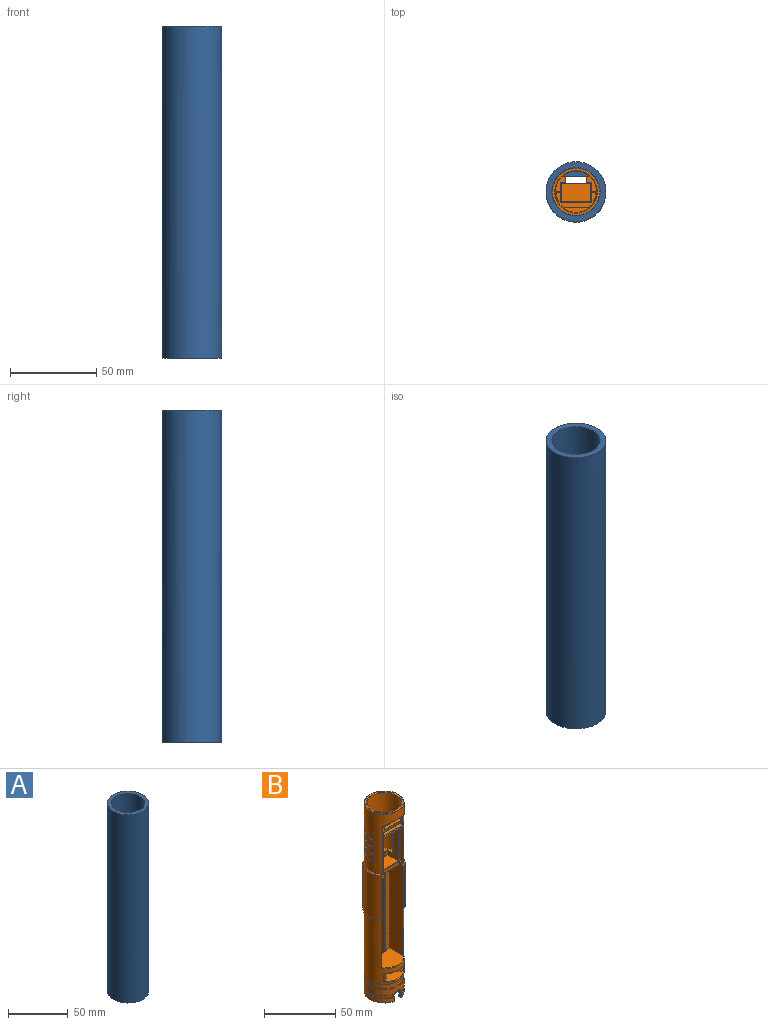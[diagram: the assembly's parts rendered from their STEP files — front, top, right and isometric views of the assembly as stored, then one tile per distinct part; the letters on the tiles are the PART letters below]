
ASSEMBLY  parts=2 mates=1
PART A: 13 faces, bbox 34.8x34.8x192.8 mm
  f0: plane 34.8x34.8mm, normal (0,0,1), area 335.4mm2, adj f2,f6
  f1: plane 34.8x34.8mm, normal (0,0,-1), area 335.4mm2, adj f2,f3
  f2: cylinder r=17.4mm len=192.8mm, axis (0,0,-1), area 21078.3mm2, adj f0,f1
  f3: cylinder r=14mm len=70.8mm, axis (0,0,-1), area 6157.8mm2, adj f1,f5,f8,f9,f10
  f4: plane 30x27.56mm, normal (0,0,-1), area 73.7mm2, adj f6,f7,f9,f10
  f5: plane 30x27.56mm, normal (0,0,1), area 73.7mm2, adj f3,f7,f9,f10
  f6: cylinder r=14mm len=82mm, axis (0,0,-1), area 7143mm2, adj f0,f4,f9,f10,f11
  f7: cylinder r=15mm len=40mm, axis (0,0,-1), area 3075.9mm2, adj f4,f5,f9,f10
  f8: plane 16.4x5mm, normal (0,0,-1), area 68.1mm2, adj f3,f9,f10,f12
  f9: plane 48x3.56mm, normal (1,0,0), area 161.2mm2, adj f3,f4,f5,f6,f7,f8,f11,f12
  f10: plane 48x3.56mm, normal (-1,0,0), area 161.2mm2, adj f3,f4,f5,f6,f7,f8,f11,f12
  f11: plane 16.4x5mm, normal (0,0,1), area 68.1mm2, adj f6,f9,f10,f12
  f12: plane 48x16.4mm, normal (0,-1,0), area 787.2mm2, adj f8,f9,f10,f11
PART B: 347 faces, bbox 32.7x30.6x163.1 mm
  f0: plane 19.04x13.2mm, normal (0,0,1), area 141.9mm2, adj f1,f335,f336,f337,f338,f339,f340,f341
  f1: plane 5.3x1.2mm, normal (0,-1,0), area 6.3mm2, adj f0,f2,f334,f335,f346
  f2: plane 15.83x14.74mm, normal (0,0,-1), area 142mm2, adj f1,f3,f4,f5,f330,f331,f332,f333
  f3: cylinder r=0.4mm len=0.86mm, axis (0,1,0), area 0.5mm2, adj f2,f4,f341,f342
  f4: torus R=0.6mm, axis (0,0,-1), area 0.3mm2, adj f2,f3,f5,f340
  f5: cylinder r=0.4mm len=2.2mm, axis (-0.92,-0.38,0), area 1.4mm2, adj f2,f4,f6,f339
  f6: bspline ~1.04x0.59mm, area 0.3mm2, adj f5,f7,f330,f339
  f7: bspline ~3.83x3.71mm, area 1.2mm2, adj f6,f8,f329,f339
  f8: bspline ~1.16x0.58mm, area 0.3mm2, adj f7,f9,f14,f15
  f9: torus R=13.6mm, axis (0,0,-1), area 6.7mm2, adj f8,f10,f15,f329
  f10: bspline ~0.97x0.62mm, area 0.3mm2, adj f9,f11,f12,f15
  f11: cylinder r=0.4mm len=7.05mm, axis (0,0,-1), area 3.3mm2, adj f10,f15,f337,f338
  f12: bspline ~3.83x3.71mm, area 1.2mm2, adj f10,f13,f329,f337
  f13: bspline ~0.97x0.58mm, area 0.3mm2, adj f12,f330,f331,f337
  f14: cylinder r=0.4mm len=7.05mm, axis (0,0,-1), area 3.3mm2, adj f8,f15,f338,f339
  f15: cylinder r=14mm len=54.5mm, axis (0,0,-1), area 3271.3mm2, adj f8,f9,f10,f11,f14,f16,f316,f317
  f16: bspline ~13.19x12.82mm, area 28.6mm2, adj f15,f17
  f17: cylinder r=6mm len=12mm, axis (0,-1,0), area 77.9mm2, adj f16,f18,f311,f312,f313,f314,f315
  f18: bspline ~2.39x0.46mm, area 0.4mm2, adj f17,f19,f315
  f19: plane 102.47x6.27mm, normal (-1,0,0), area 424.5mm2, adj f18,f20,f295,f296,f297,f306,f307,f308
  f20: cylinder r=0.4mm len=1.61mm, axis (0,-1,0), area 0.8mm2, adj f19,f21,f294,f310
  f21: plane 21.42x18.8mm, normal (0,0,1), area 349.1mm2, adj f20,f22,f290,f291,f292,f293,f294,f325
  f22: plane 77.6x14mm, normal (-1,0,0), area 1050.7mm2, adj f21,f23,f287,f288,f289,f293,f327
  f23: cylinder r=0.4mm len=21.1mm, axis (1,0,0), area 13.3mm2, adj f22,f24,f287,f290,f291,f293
  f24: plane 12.8x3mm, normal (0,1,0), area 38.4mm2, adj f23,f25,f286,f310
  f25: cylinder r=0.2mm len=17.2mm, axis (1,0,0), area 5.4mm2, adj f24,f26,f282,f283,f284,f285
  f26: plane 36.8x11.2mm, normal (-1,0,0), area 213mm2, adj f25,f27,f273,f274,f275,f276,f277,f278
  f27: cylinder r=0.2mm len=5.8mm, axis (0,1,0), area 1.7mm2, adj f26,f28,f30,f273
  f28: cylinder r=0.2mm len=2.4mm, axis (-1,0,0), area 0.7mm2, adj f27,f29,f30,f285
  f29: torus R=0.2mm, axis (0,0,1), area 0.2mm2, adj f28,f30,f309,f310
  f30: plane 8.85x5.79mm, normal (0,0,1), area 26.5mm2, adj f27,f28,f29,f31,f269,f270,f271,f272
  f31: cylinder r=0.4mm len=32.6mm, axis (0,0,1), area 20.9mm2, adj f30,f32,f269,f272
  f32: bspline ~0.98x0.97mm, area 0.6mm2, adj f31,f33,f268,f272
  f33: cylinder r=0.4mm len=2.59mm, axis (-1,0,0), area 1.6mm2, adj f32,f34,f267,f269
  f34: plane 23.19x8.4mm, normal (0,0,1), area 65.2mm2, adj f33,f35,f263,f264,f265,f266,f268,f274
  f35: cylinder r=0.4mm len=15.11mm, axis (-1,0,0), area 9.5mm2, adj f34,f36,f261,f262
  f36: plane 80.11x23.32mm, normal (0,-1,0), area 142.8mm2, adj f35,f37,f45,f48,f49,f50,f54,f55
  f37: cylinder r=0.4mm len=3.6mm, axis (0,0,1), area 2.1mm2, adj f36,f38,f44,f45
  f38: plane 3.2x3.2mm, normal (-1,0,0), area 9mm2, adj f37,f39,f43,f44,f45
  f39: plane 17.2x2.8mm, normal (0,-1,0), area 48.2mm2, adj f38,f40,f42,f43
  f40: cylinder r=0.4mm len=18mm, axis (1,0,0), area 11.1mm2, adj f39,f41,f44,f287
  f41: cylinder r=0.4mm len=3.6mm, axis (0,1,0), area 2mm2, adj f40,f42,f55,f287
  f42: plane 3.2x3.2mm, normal (1,0,0), area 9mm2, adj f39,f41,f43,f54,f55
  f43: cylinder r=0.4mm len=17.2mm, axis (-1,0,0), area 10.8mm2, adj f38,f39,f42,f282
  f44: cylinder r=0.4mm len=3.6mm, axis (0,-1,0), area 2mm2, adj f37,f38,f40,f287
  f45: plane 3.6x1.8mm, normal (0,0,1), area 4.5mm2, adj f36,f37,f38,f46,f47,f48,f281
  f46: plane 30x1mm, normal (0,-1,0), area 30mm2, adj f45,f47,f280,f281
  f47: plane 30x2.8mm, normal (-1,0,0), area 84.1mm2, adj f45,f46,f48,f280
  f48: cylinder r=0.4mm len=30.4mm, axis (0,0,-1), area 19mm2, adj f36,f45,f47,f49
  f49: cylinder r=0.4mm len=20.8mm, axis (1,0,0), area 12.8mm2, adj f36,f48,f50,f280
  f50: cylinder r=0.4mm len=30.4mm, axis (0,0,1), area 19mm2, adj f36,f49,f51,f54
  f51: plane 30x2.8mm, normal (1,0,0), area 84.1mm2, adj f50,f52,f54,f280
  f52: plane 30x1mm, normal (0,-1,0), area 30mm2, adj f51,f53,f54,f280
  f53: cylinder r=0.4mm len=30mm, axis (0,0,-1), area 18.8mm2, adj f52,f54,f280,f283
  f54: plane 3.6x1.8mm, normal (0,0,1), area 4.5mm2, adj f36,f42,f50,f51,f52,f53,f55
  f55: cylinder r=0.4mm len=3.6mm, axis (0,0,-1), area 2.1mm2, adj f36,f41,f42,f54
  f56: cylinder r=0.4mm len=35.78mm, axis (0,0,-1), area 22.5mm2, adj f36,f57,f287,f290
  f57: sphere r=0.4mm, area 0.2mm2, adj f56,f58,f59
  f58: bspline ~4.34x3.12mm, area 0.7mm2, adj f57,f290,f324,f325
  f59: bspline ~5.05x4.14mm, area 0.4mm2, adj f36,f57,f60,f324
  f60: sphere r=0.4mm, area 0.1mm2, adj f59,f61,f201
  f61: torus R=14.6mm, axis (0,0,-1), area 7.5mm2, adj f60,f62,f200,f324
  f62: sphere r=0.4mm, area 0.2mm2, adj f61,f63,f199
  f63: cylinder r=0.4mm len=37.67mm, axis (0,0,-1), area 33.2mm2, adj f62,f64,f197,f200
  f64: plane 48x2.8mm, normal (1,0,0), area 122.5mm2, adj f63,f65,f193,f194,f195,f196,f199,f322
  f65: plane 16.57x4.65mm, normal (0,0,1), area 41.4mm2, adj f64,f66,f178,f179,f191,f192,f193,f307
  f66: cylinder r=0.2mm len=1.99mm, axis (0,1,0), area 0.5mm2, adj f65,f67,f178,f192
  f67: plane 102.47x6.27mm, normal (1,0,0), area 424.5mm2, adj f66,f68,f166,f178,f286,f292,f295,f297
  f68: cylinder r=0.4mm len=6.4mm, axis (0,-1,0), area 3.8mm2, adj f67,f69,f79,f80
  f69: plane 24x22.15mm, normal (0,0,-1), area 317.6mm2, adj f68,f70,f73,f74,f76,f79,f80,f296
  f70: cylinder r=0.4mm len=1.85mm, axis (1,0,0), area 1mm2, adj f69,f71,f295,f296
  f71: sphere r=0.4mm, area 0.2mm2, adj f70,f72,f73
  f72: cylinder r=0.4mm len=11.65mm, axis (0,0,1), area 7.2mm2, adj f71,f295,f333,f346
  f73: cylinder r=0.4mm len=4.39mm, axis (0,1,0), area 2.6mm2, adj f69,f71,f74,f346
  f74: cylinder r=0.4mm len=9.1mm, axis (1,0,0), area 5.5mm2, adj f69,f73,f75,f76
  f75: plane 8.3x5.55mm, normal (0,1,0), area 46.1mm2, adj f74,f344,f345,f346
  f76: cylinder r=0.4mm len=4.39mm, axis (0,-1,0), area 2.6mm2, adj f69,f74,f77,f344
  f77: sphere r=0.4mm, area 0.2mm2, adj f76,f78,f79
  f78: cylinder r=0.4mm len=11.65mm, axis (0,0,-1), area 7.2mm2, adj f77,f295,f333,f344
  f79: cylinder r=0.4mm len=1.85mm, axis (1,0,0), area 1mm2, adj f68,f69,f77,f295
  f80: cylinder r=12mm len=24mm, axis (0,0,-1), area 778mm2, adj f68,f69,f81,f158,f159,f160,f161,f162
  f81: cylinder r=0.4mm len=4.6mm, axis (0,0,-1), area 2.4mm2, adj f80,f82,f157,f165
  f82: sphere r=0.4mm, area 0.1mm2, adj f81,f83,f159
  f83: cylinder r=0.4mm len=1.24mm, axis (0,-1,0), area 0.8mm2, adj f82,f84,f85,f156,f157
  f84: sphere r=0.4mm, area 0mm2, adj f83,f159
  f85: plane 26.34x10.2mm, normal (0,0,-1), area 40.8mm2, adj f83,f86,f155,f159
  f86: cylinder r=0.4mm len=1.24mm, axis (0,-1,0), area 0.8mm2, adj f85,f87,f153,f154
  f87: plane 4.6x1.24mm, normal (1,0,0), area 4.9mm2, adj f86,f88,f150,f151,f152,f160
  f88: cylinder r=0.4mm len=3.3mm, axis (0,0,-1), area 2.4mm2, adj f87,f89,f148,f149,f153
  f89: cylinder r=14mm len=27.11mm, axis (0,0,-1), area 121.8mm2, adj f88,f90,f147,f155
  f90: torus R=13.7mm, axis (0,0,-1), area 17.3mm2, adj f89,f91,f146,f149
  f91: plane 26.54x10.3mm, normal (0,0,1), area 10.7mm2, adj f90,f92,f143,f144,f146,f149,f151,f152
  f92: cylinder r=13.4mm len=25.95mm, axis (0,0,1), area 70.2mm2, adj f91,f93,f141,f142,f143,f151
  f93: bspline ~2.51x0.94mm, area 0.8mm2, adj f92,f94,f141,f150,f151
  f94: cylinder r=0.4mm len=0.7mm, axis (0,-1,0), area 0.2mm2, adj f93,f95,f141,f150
  f95: bspline ~0.43x0.38mm, area 0.1mm2, adj f94,f96,f140
  f96: bspline ~6.78x2.7mm, area 4.9mm2, adj f95,f97,f134,f135,f140,f150
  f97: bspline ~0.43x0.38mm, area 0.1mm2, adj f96,f98,f134
  f98: cylinder r=0.4mm len=0.7mm, axis (0,-1,0), area 0.2mm2, adj f97,f99,f133,f150
  f99: bspline ~2.51x0.94mm, area 0.8mm2, adj f98,f100,f132,f133,f150
  f100: cylinder r=13.4mm len=25.95mm, axis (0,0,1), area 70.2mm2, adj f99,f101,f130,f131,f132,f133
  f101: plane 26.54x10.4mm, normal (0,0,1), area 10.8mm2, adj f100,f102,f126,f127,f128,f129,f130,f132
  f102: cylinder r=0.3mm len=0.62mm, axis (0,1,0), area 0.2mm2, adj f101,f103,f126,f132
  f103: plane 4.6x1.24mm, normal (-1,0,0), area 4.9mm2, adj f102,f104,f125,f132,f150,f162
  f104: cylinder r=0.4mm len=1.24mm, axis (0,1,0), area 0.8mm2, adj f103,f105,f106,f124
  f105: sphere r=0.4mm, area 0.1mm2, adj f104,f162,f163
  f106: plane 26.34x10.2mm, normal (0,0,-1), area 40.8mm2, adj f104,f107,f123,f163
  f107: cylinder r=0.4mm len=1.24mm, axis (0,1,0), area 0.8mm2, adj f106,f108,f109,f122
  f108: sphere r=0.4mm, area 0.3mm2, adj f107,f163,f164
  f109: plane 4.6x1.24mm, normal (-1,0,0), area 4.9mm2, adj f107,f110,f120,f129,f130,f164
  f110: cylinder r=3mm len=6mm, axis (0,-1,0), area 10mm2, adj f109,f111,f115,f119,f131,f142,f157,f165
  f111: cylinder r=0.4mm len=0.7mm, axis (0,-1,0), area 0.2mm2, adj f110,f112,f131,f133
  f112: bspline ~0.43x0.38mm, area 0.1mm2, adj f111,f113,f115
  f113: bspline ~0.36x0.33mm, area 0.1mm2, adj f112,f114,f115,f133
  f114: torus R=13.7mm, axis (0,0,-1), area 17.5mm2, adj f113,f133,f134,f135
  f115: bspline ~6.78x2.7mm, area 4.9mm2, adj f110,f112,f113,f116,f117,f135
  f116: bspline ~0.43x0.38mm, area 0.1mm2, adj f115,f117,f119
  f117: bspline ~0.41x0.33mm, area 0.1mm2, adj f115,f116,f118,f141
  f118: torus R=13.7mm, axis (0,0,-1), area 17.5mm2, adj f117,f135,f140,f141
  f119: cylinder r=0.4mm len=0.7mm, axis (0,-1,0), area 0.2mm2, adj f110,f116,f141,f142
  f120: cylinder r=0.4mm len=3.3mm, axis (0,0,-1), area 2.4mm2, adj f109,f121,f122,f128
  f121: cylinder r=14mm len=27.11mm, axis (0,0,-1), area 121.8mm2, adj f120,f123,f125,f127
  f122: sphere r=0.4mm, area 0.4mm2, adj f107,f120,f123
  f123: torus R=13.6mm, axis (0,0,-1), area 22.9mm2, adj f106,f121,f122,f124
  f124: sphere r=0.4mm, area 0.3mm2, adj f104,f123,f125
  f125: cylinder r=0.4mm len=3.3mm, axis (0,0,-1), area 2.4mm2, adj f103,f121,f124,f126
  f126: torus R=0.1mm, axis (0,0,-1), area 0.3mm2, adj f101,f102,f125,f127
  f127: torus R=13.7mm, axis (0,0,-1), area 17.3mm2, adj f101,f121,f126,f128
  f128: torus R=0.1mm, axis (0,0,-1), area 0.3mm2, adj f101,f120,f127,f129
  f129: cylinder r=0.3mm len=0.62mm, axis (0,1,0), area 0.2mm2, adj f101,f109,f128,f130
  f130: cylinder r=0.4mm len=1.3mm, axis (0,0,1), area 0.8mm2, adj f100,f101,f109,f129,f131
  f131: bspline ~2.51x0.94mm, area 0.8mm2, adj f100,f110,f111,f130,f133
  f132: cylinder r=0.4mm len=1.3mm, axis (0,0,1), area 0.8mm2, adj f99,f100,f101,f102,f103
  f133: plane 26.68x10.61mm, normal (0,0,-1), area 10.9mm2, adj f98,f99,f100,f111,f113,f114,f131,f134
  f134: bspline ~0.41x0.33mm, area 0.1mm2, adj f96,f97,f114,f133
  f135: cylinder r=14mm len=28mm, axis (0,0,-1), area 475mm2, adj f96,f114,f115,f118,f136
  f136: torus R=13.7mm, axis (0,0,-1), area 41.1mm2, adj f135,f137
  f137: plane 27.4x27.4mm, normal (0,0,1), area 25.5mm2, adj f136,f138
  f138: cylinder r=13.4mm len=26.8mm, axis (0,0,1), area 336.8mm2, adj f137,f139
  f139: plane 27.4x27.4mm, normal (0,0,-1), area 25.5mm2, adj f138,f323
  f140: bspline ~0.36x0.33mm, area 0.1mm2, adj f95,f96,f118,f141
  f141: plane 26.68x10.61mm, normal (0,0,-1), area 10.9mm2, adj f92,f93,f94,f117,f118,f119,f140,f142
  f142: bspline ~2.51x0.94mm, area 0.8mm2, adj f92,f110,f119,f141,f143
  f143: cylinder r=0.4mm len=1.4mm, axis (0,0,1), area 0.8mm2, adj f91,f92,f142,f144,f157
  f144: cylinder r=0.4mm len=0.72mm, axis (0,-1,0), area 0.3mm2, adj f91,f143,f145,f157
  f145: bspline ~0.49x0.4mm, area 0.1mm2, adj f144,f146,f147
  f146: torus R=0.1mm, axis (0,0,-1), area 0mm2, adj f90,f91,f145,f147
  f147: cylinder r=0.4mm len=3.3mm, axis (0,0,-1), area 2.4mm2, adj f89,f145,f146,f156,f157
  f148: bspline ~0.49x0.4mm, area 0.1mm2, adj f88,f149,f152
  f149: torus R=0.1mm, axis (0,0,-1), area 0mm2, adj f88,f90,f91,f148
  f150: cylinder r=3mm len=6mm, axis (0,-1,0), area 10mm2, adj f87,f93,f94,f96,f98,f99,f103,f161
  f151: cylinder r=0.4mm len=1.4mm, axis (0,0,1), area 0.8mm2, adj f87,f91,f92,f93,f152
  f152: cylinder r=0.4mm len=0.72mm, axis (0,-1,0), area 0.3mm2, adj f87,f91,f148,f151
  f153: sphere r=0.4mm, area 0.2mm2, adj f86,f88,f155
  f154: sphere r=0.4mm, area 0.3mm2, adj f86,f159,f160
  f155: torus R=13.6mm, axis (0,0,-1), area 22.9mm2, adj f85,f89,f153,f156
  f156: sphere r=0.4mm, area 0.4mm2, adj f83,f147,f155
  f157: plane 4.6x1.24mm, normal (1,0,0), area 4.9mm2, adj f81,f83,f110,f143,f144,f147
  f158: plane 12x1.61mm, normal (0,0,-1), area 13mm2, adj f80,f297
  f159: torus R=12.4mm, axis (0,0,-1), area 19.7mm2, adj f80,f82,f84,f85,f154
  f160: cylinder r=0.4mm len=4.6mm, axis (0,0,-1), area 2.4mm2, adj f80,f87,f154,f161
  f161: bspline ~6.58x4.15mm, area 5.6mm2, adj f80,f150,f160,f162
  f162: cylinder r=0.4mm len=4.6mm, axis (0,0,-1), area 2.4mm2, adj f80,f103,f105,f161
  f163: torus R=12.4mm, axis (0,0,-1), area 19.7mm2, adj f80,f105,f106,f108
  f164: cylinder r=0.4mm len=4.6mm, axis (0,0,-1), area 2.4mm2, adj f80,f108,f109,f165
  f165: bspline ~6.58x4.15mm, area 5.6mm2, adj f80,f81,f110,f164
  f166: cylinder r=0.2mm len=3mm, axis (0,-1,0), area 0.9mm2, adj f67,f167,f176,f177
  f167: plane 8.85x5.79mm, normal (0,0,1), area 26.5mm2, adj f166,f168,f169,f170,f172,f173,f175,f176
  f168: cylinder r=0.2mm len=2.4mm, axis (-1,0,0), area 0.7mm2, adj f167,f169,f177,f284
  f169: cylinder r=0.2mm len=5.8mm, axis (0,1,0), area 1.7mm2, adj f167,f168,f170,f283
  f170: cylinder r=0.4mm len=32.8mm, axis (0,0,1), area 20.5mm2, adj f167,f169,f171,f172,f283
  f171: sphere r=0.4mm, area 0.3mm2, adj f170,f264,f265
  f172: plane 32.6x2.59mm, normal (0,1,0), area 84.5mm2, adj f167,f170,f173,f264
  f173: cylinder r=0.4mm len=32.6mm, axis (0,0,1), area 20.9mm2, adj f167,f172,f174,f272
  f174: bspline ~1.01x0.94mm, area 0.6mm2, adj f173,f263,f264,f272
  f175: cylinder r=0.2mm len=1.76mm, axis (1,0,0), area 0.5mm2, adj f167,f176,f193,f272
  f176: torus R=0.2mm, axis (0,0,1), area 0.2mm2, adj f166,f167,f175,f178
  f177: torus R=0.2mm, axis (0,0,1), area 0.2mm2, adj f166,f167,f168,f286
  f178: cylinder r=0.4mm len=48mm, axis (0,0,-1), area 30.1mm2, adj f65,f66,f67,f176,f193
  f179: plane 48x2.8mm, normal (-1,0,0), area 122.5mm2, adj f65,f180,f187,f188,f190,f191,f194,f320
  f180: cylinder r=0.4mm len=37.67mm, axis (0,0,-1), area 33.2mm2, adj f179,f181,f184,f186
  f181: sphere r=0.4mm, area 0.2mm2, adj f180,f182,f190
  f182: torus R=14.6mm, axis (0,0,-1), area 7.5mm2, adj f181,f183,f184,f328
  f183: sphere r=0.4mm, area 0.1mm2, adj f182,f249,f250
  f184: cylinder r=15mm len=37.67mm, axis (0,0,-1), area 897.3mm2, adj f180,f182,f185,f249
  f185: torus R=14.6mm, axis (0,0,1), area 7.5mm2, adj f184,f186,f248,f249
  f186: sphere r=0.4mm, area 0.3mm2, adj f180,f185,f187
  f187: bspline ~5.08x4.26mm, area 1.2mm2, adj f179,f186,f188,f248
  f188: cylinder r=0.4mm len=4.57mm, axis (0,0,-1), area 3.7mm2, adj f179,f187,f189,f194,f208,f248
  f189: torus R=13.6mm, axis (0,0,1), area 11.7mm2, adj f188,f194,f195,f208
  f190: bspline ~5.08x4.26mm, area 1.2mm2, adj f179,f181,f320,f328
  f191: plane 48x1.8mm, normal (0,1,0), area 86.1mm2, adj f65,f179,f194,f271,f272,f308
  f192: cylinder r=0.2mm len=12.4mm, axis (1,0,0), area 3.8mm2, adj f65,f66,f306,f307
  f193: plane 48x1.8mm, normal (0,1,0), area 86.1mm2, adj f64,f65,f175,f178,f194,f272
  f194: plane 16.57x4.6mm, normal (0,0,-1), area 28.5mm2, adj f64,f179,f188,f189,f191,f193,f195,f272
  f195: cylinder r=0.4mm len=4.57mm, axis (0,0,-1), area 3.7mm2, adj f64,f189,f194,f196,f202,f208
  f196: bspline ~5.08x4.26mm, area 1.2mm2, adj f64,f195,f197,f202
  f197: sphere r=0.4mm, area 0.3mm2, adj f63,f196,f198
  f198: torus R=14.6mm, axis (0,0,1), area 7.5mm2, adj f197,f200,f201,f202
  f199: bspline ~5.08x4.26mm, area 1.2mm2, adj f62,f64,f322,f324
  f200: cylinder r=15mm len=37.67mm, axis (0,0,-1), area 897.3mm2, adj f61,f63,f198,f201
  f201: cylinder r=0.4mm len=37.99mm, axis (0,0,-1), area 14mm2, adj f36,f60,f198,f200,f202
  f202: cone r=14mm half-angle=45deg, axis (0,0,-1), area 29mm2, adj f36,f195,f196,f198,f201,f208
  f203: cylinder r=0.4mm len=3.17mm, axis (0,0,1), area 2.8mm2, adj f36,f204,f206,f261,f272
  f204: bspline ~17.47x4.15mm, area 17.8mm2, adj f203,f205,f206,f272
  f205: cylinder r=0.4mm len=3.17mm, axis (0,0,1), area 2.8mm2, adj f36,f204,f206,f262,f272
  f206: plane 20.52x4.69mm, normal (0,-0.68,-0.73), area 34.6mm2, adj f36,f203,f204,f205,f207
  f207: bspline ~21.19x4.85mm, area 9.5mm2, adj f36,f206,f208
  f208: cylinder r=14mm len=51.6mm, axis (0,0,-1), area 2458.5mm2, adj f36,f188,f189,f195,f202,f207,f209,f215
  f209: cylinder r=0.3mm len=4.6mm, axis (0,0,-1), area 2mm2, adj f208,f210,f213,f214,f215,f217
  f210: plane 27.4x17.25mm, normal (0,0,1), area 14.9mm2, adj f209,f211,f212,f214,f215,f216
  f211: cylinder r=13.4mm len=26.8mm, axis (0,0,1), area 196.5mm2, adj f210,f212,f213,f214
  f212: plane 4x0.29mm, normal (-0.26,0.97,0), area 1.2mm2, adj f210,f211,f213,f216
  f213: plane 27.4x17.25mm, normal (0,0,-1), area 14.9mm2, adj f209,f211,f212,f214,f216,f217
  f214: plane 4x0.29mm, normal (0.26,0.97,0), area 1.2mm2, adj f209,f210,f211,f213
  f215: torus R=13.7mm, axis (0,0,-1), area 24.1mm2, adj f208,f209,f210,f216
  f216: cylinder r=0.3mm len=4.6mm, axis (0,0,-1), area 2mm2, adj f208,f210,f212,f213,f215,f217
  f217: torus R=13.7mm, axis (0,0,-1), area 24.1mm2, adj f208,f209,f213,f216
  f218: cylinder r=0.3mm len=4.6mm, axis (0,0,-1), area 2mm2, adj f208,f219,f222,f223,f224,f226
  f219: plane 27.4x17.25mm, normal (0,0,1), area 14.9mm2, adj f218,f220,f221,f223,f224,f225
  f220: cylinder r=13.4mm len=26.8mm, axis (0,0,1), area 196.5mm2, adj f219,f221,f222,f223
  f221: plane 4x0.29mm, normal (-0.26,0.97,0), area 1.2mm2, adj f219,f220,f222,f225
  f222: plane 27.4x17.25mm, normal (0,0,-1), area 14.9mm2, adj f218,f220,f221,f223,f225,f226
  f223: plane 4x0.29mm, normal (0.26,0.97,0), area 1.2mm2, adj f218,f219,f220,f222
  f224: torus R=13.7mm, axis (0,0,-1), area 24.1mm2, adj f208,f218,f219,f225
  f225: cylinder r=0.3mm len=4.6mm, axis (0,0,-1), area 2mm2, adj f208,f219,f221,f222,f224,f226
  f226: torus R=13.7mm, axis (0,0,-1), area 24.1mm2, adj f208,f218,f222,f225
  f227: cylinder r=0.3mm len=4.6mm, axis (0,0,-1), area 2mm2, adj f208,f228,f231,f232,f233,f235
  f228: plane 27.4x17.25mm, normal (0,0,1), area 14.9mm2, adj f227,f229,f230,f232,f233,f234
  f229: cylinder r=13.4mm len=26.8mm, axis (0,0,1), area 196.5mm2, adj f228,f230,f231,f232
  f230: plane 4x0.29mm, normal (-0.26,0.97,0), area 1.2mm2, adj f228,f229,f231,f234
  f231: plane 27.4x17.25mm, normal (0,0,-1), area 14.9mm2, adj f227,f229,f230,f232,f234,f235
  f232: plane 4x0.29mm, normal (0.26,0.97,0), area 1.2mm2, adj f227,f228,f229,f231
  f233: torus R=13.7mm, axis (0,0,-1), area 24.1mm2, adj f208,f227,f228,f234
  f234: cylinder r=0.3mm len=4.6mm, axis (0,0,-1), area 2mm2, adj f208,f228,f230,f231,f233,f235
  f235: torus R=13.7mm, axis (0,0,-1), area 24.1mm2, adj f208,f227,f231,f234
  f236: cylinder r=0.3mm len=4.6mm, axis (0,0,-1), area 2mm2, adj f208,f237,f240,f241,f242,f244
  f237: plane 27.4x17.25mm, normal (0,0,1), area 14.9mm2, adj f236,f238,f239,f241,f242,f243
  f238: cylinder r=13.4mm len=26.8mm, axis (0,0,1), area 196.5mm2, adj f237,f239,f240,f241
  f239: plane 4x0.29mm, normal (-0.26,0.97,0), area 1.2mm2, adj f237,f238,f240,f243
  f240: plane 27.4x17.25mm, normal (0,0,-1), area 14.9mm2, adj f236,f238,f239,f241,f243,f244
  f241: plane 4x0.29mm, normal (0.26,0.97,0), area 1.2mm2, adj f236,f237,f238,f240
  f242: torus R=13.7mm, axis (0,0,-1), area 24.1mm2, adj f208,f236,f237,f243
  f243: cylinder r=0.3mm len=4.6mm, axis (0,0,-1), area 2mm2, adj f208,f237,f239,f240,f242,f244
  f244: torus R=13.7mm, axis (0,0,-1), area 24.1mm2, adj f208,f236,f240,f243
  f245: torus R=13.6mm, axis (0,0,1), area 54.7mm2, adj f208,f246
  f246: plane 27.2x27.2mm, normal (0,0,1), area 98mm2, adj f245,f247
  f247: torus R=12.4mm, axis (0,0,1), area 47.9mm2, adj f246,f272
  f248: cone r=14mm half-angle=45deg, axis (0,0,-1), area 29mm2, adj f36,f185,f187,f188,f208,f249
  f249: cylinder r=0.4mm len=37.99mm, axis (0,0,-1), area 14mm2, adj f36,f183,f184,f185,f248
  f250: bspline ~5.05x4.14mm, area 0.4mm2, adj f36,f183,f251,f328
  f251: sphere r=0.4mm, area 0.2mm2, adj f250,f288,f289
  f252: cylinder r=0.4mm len=20.8mm, axis (-1,0,0), area 12.8mm2, adj f36,f253,f257,f278
  f253: cylinder r=0.4mm len=3.8mm, axis (0,0,-1), area 2.1mm2, adj f36,f252,f254,f256
  f254: plane 3x2.8mm, normal (-1,0,0), area 8.4mm2, adj f253,f255,f276,f278
  f255: plane 3x1mm, normal (0,-1,0), area 3mm2, adj f254,f276,f277,f278
  f256: cylinder r=0.4mm len=20.8mm, axis (1,0,0), area 12.8mm2, adj f36,f253,f257,f276
  f257: cylinder r=0.4mm len=3.8mm, axis (0,0,1), area 2.1mm2, adj f36,f252,f256,f258
  f258: plane 3x2.8mm, normal (1,0,0), area 8.4mm2, adj f257,f259,f276,f278
  f259: plane 3x1mm, normal (0,-1,0), area 3mm2, adj f258,f260,f276,f278
  f260: cylinder r=0.4mm len=3mm, axis (0,0,-1), area 1.9mm2, adj f259,f276,f278,f283
  f261: bspline ~1.6x0.95mm, area 0.9mm2, adj f35,f36,f203,f263
  f262: bspline ~1.43x0.95mm, area 0.9mm2, adj f35,f36,f205,f268
  f263: torus R=11.6mm, axis (0,0,1), area 5.9mm2, adj f34,f174,f261,f272
  f264: cylinder r=0.4mm len=2.59mm, axis (-1,0,0), area 1.6mm2, adj f34,f171,f172,f174
  f265: cylinder r=0.4mm len=6mm, axis (0,-1,0), area 3.6mm2, adj f34,f171,f266,f283
  f266: cylinder r=0.4mm len=18mm, axis (1,0,0), area 11.1mm2, adj f34,f265,f274,f275
  f267: sphere r=0.4mm, area 0.4mm2, adj f33,f273,f274
  f268: torus R=11.6mm, axis (0,0,1), area 5.9mm2, adj f32,f34,f262,f272
  f269: plane 32.6x2.59mm, normal (0,1,0), area 84.5mm2, adj f30,f31,f33,f273
  f270: torus R=0.2mm, axis (0,0,1), area 0.2mm2, adj f30,f271,f308,f309
  f271: cylinder r=0.2mm len=1.76mm, axis (1,0,0), area 0.5mm2, adj f30,f191,f270,f272
  f272: cylinder r=12mm len=47.8mm, axis (0,0,1), area 2201.7mm2, adj f30,f31,f32,f167,f173,f174,f175,f191
  f273: cylinder r=0.4mm len=32.8mm, axis (0,0,-1), area 20.5mm2, adj f26,f27,f30,f267,f269
  f274: cylinder r=0.4mm len=6mm, axis (0,1,0), area 3.6mm2, adj f26,f34,f266,f267
  f275: plane 17.2x1.6mm, normal (0,1,0), area 27.5mm2, adj f26,f266,f276,f283
  f276: plane 20x3.2mm, normal (0,0,-1), area 56.1mm2, adj f26,f254,f255,f256,f258,f259,f260,f275
  f277: cylinder r=0.4mm len=3mm, axis (0,0,-1), area 1.9mm2, adj f26,f255,f276,f278
  f278: plane 20x3.2mm, normal (0,0,1), area 56.1mm2, adj f26,f252,f254,f255,f258,f259,f260,f277
  f279: plane 17.2x2mm, normal (0,1,0), area 34.4mm2, adj f26,f278,f280,f283
  f280: plane 20x3.2mm, normal (0,0,-1), area 56.1mm2, adj f26,f46,f47,f49,f51,f52,f53,f279
  f281: cylinder r=0.4mm len=30mm, axis (0,0,-1), area 18.8mm2, adj f26,f45,f46,f280
  f282: plane 17.2x10.6mm, normal (0,0,1), area 182.3mm2, adj f25,f26,f43,f283
  f283: plane 36.8x11.2mm, normal (1,0,0), area 213mm2, adj f25,f53,f169,f170,f260,f265,f275,f276
  f284: plane 4x2.2mm, normal (0,-1,0), area 8.8mm2, adj f25,f168,f283,f286
  f285: plane 4x2.2mm, normal (0,-1,0), area 8.8mm2, adj f25,f26,f28,f310
  f286: cylinder r=0.4mm len=85mm, axis (0,0,1), area 53.3mm2, adj f24,f67,f177,f284,f291,f292
  f287: plane 21.9x14mm, normal (0,0,-1), area 230.7mm2, adj f22,f23,f36,f40,f41,f44,f56,f288
  f288: cylinder r=0.4mm len=35.78mm, axis (0,0,1), area 22.5mm2, adj f22,f36,f251,f287
  f289: bspline ~4.34x3.12mm, area 0.7mm2, adj f22,f251,f327,f328
  f290: plane 77.6x14mm, normal (1,0,0), area 1050.7mm2, adj f21,f23,f56,f58,f287,f291,f325
  f291: plane 77.6x4.15mm, normal (0,-1,0), area 322mm2, adj f21,f23,f286,f290
  f292: cylinder r=0.4mm len=1.61mm, axis (0,1,0), area 0.8mm2, adj f21,f67,f286,f294
  f293: plane 77.6x4.15mm, normal (0,-1,0), area 322mm2, adj f21,f22,f23,f310
  f294: cylinder r=0.4mm len=12.8mm, axis (-1,0,0), area 7.8mm2, adj f20,f21,f292,f295
  f295: plane 17.2x12mm, normal (0,1,0), area 100.4mm2, adj f19,f67,f70,f72,f78,f79,f294,f333
  f296: cylinder r=0.4mm len=6.4mm, axis (0,1,0), area 3.8mm2, adj f19,f69,f70,f80
  f297: plane 34.17x12mm, normal (0,-1,0), area 330.3mm2, adj f19,f67,f80,f158,f298,f303,f304,f305
  f298: cylinder r=0.4mm len=6.1mm, axis (0,0,1), area 3.6mm2, adj f297,f299,f303,f305
  f299: plane 5.3x2.34mm, normal (1,0,0), area 12.4mm2, adj f298,f300,f302,f316
  f300: plane 6.32x2.81mm, normal (0,0,-1), area 16.9mm2, adj f299,f301,f305,f316,f317,f318
  f301: plane 5.3x2.34mm, normal (-1,0,0), area 12.4mm2, adj f300,f302,f304,f318
  f302: plane 6.32x2.81mm, normal (0,0,1), area 16.9mm2, adj f299,f301,f303,f316,f318,f319
  f303: cylinder r=0.4mm len=7.1mm, axis (-1,0,0), area 4.2mm2, adj f297,f298,f302,f304
  f304: cylinder r=0.4mm len=6.1mm, axis (0,0,-1), area 3.6mm2, adj f297,f301,f303,f305
  f305: cylinder r=0.4mm len=7.1mm, axis (1,0,0), area 4.2mm2, adj f297,f298,f300,f304
  f306: plane 15.97x12mm, normal (0,-1,0), area 155.3mm2, adj f19,f67,f192,f312
  f307: cylinder r=0.2mm len=1.99mm, axis (0,-1,0), area 0.5mm2, adj f19,f65,f192,f308
  f308: cylinder r=0.4mm len=48mm, axis (0,0,1), area 30.1mm2, adj f19,f65,f191,f270,f307
  f309: cylinder r=0.2mm len=3mm, axis (0,1,0), area 0.9mm2, adj f19,f29,f30,f270
  f310: cylinder r=0.4mm len=85mm, axis (0,0,-1), area 53.3mm2, adj f19,f20,f24,f29,f285,f293
  f311: bspline ~2.39x0.46mm, area 0.4mm2, adj f17,f19,f312
  f312: torus R=6.4mm, axis (0,-1,0), area 9.4mm2, adj f17,f306,f311,f313
  f313: bspline ~2.39x0.46mm, area 0.4mm2, adj f17,f67,f312
  f314: bspline ~2.39x0.46mm, area 0.4mm2, adj f17,f67,f315
  f315: torus R=6.4mm, axis (0,-1,0), area 9.4mm2, adj f17,f18,f297,f314
  f316: cylinder r=0.4mm len=6.1mm, axis (0,0,-1), area 4.1mm2, adj f15,f299,f300,f302,f317,f319
  f317: torus R=13.6mm, axis (0,0,1), area 4.3mm2, adj f15,f300,f316,f318
  f318: cylinder r=0.4mm len=6.1mm, axis (0,0,-1), area 4.1mm2, adj f15,f300,f301,f302,f317,f319
  f319: torus R=13.6mm, axis (0,0,1), area 4.3mm2, adj f15,f302,f316,f318
  f320: cylinder r=0.4mm len=4.57mm, axis (0,0,-1), area 3.7mm2, adj f15,f65,f179,f190,f321,f328
  f321: torus R=13.6mm, axis (0,0,1), area 11.7mm2, adj f15,f65,f320,f322
  f322: cylinder r=0.4mm len=4.57mm, axis (0,0,-1), area 3.7mm2, adj f15,f64,f65,f199,f321,f324
  f323: torus R=13.7mm, axis (0,0,-1), area 41.1mm2, adj f15,f139
  f324: cone r=15mm half-angle=45deg, axis (0,0,1), area 28.5mm2, adj f15,f58,f59,f61,f199,f322,f325
  f325: cylinder r=0.4mm len=41.37mm, axis (0,0,-1), area 41mm2, adj f15,f21,f58,f290,f324,f326
  f326: torus R=13.6mm, axis (0,0,-1), area 16mm2, adj f15,f21,f325,f327
  f327: cylinder r=0.4mm len=41.37mm, axis (0,0,-1), area 41mm2, adj f15,f21,f22,f289,f326,f328
  f328: cone r=15mm half-angle=45deg, axis (0,0,1), area 28.5mm2, adj f15,f182,f190,f250,f289,f320,f327
  f329: cone r=12mm half-angle=45deg, axis (0,0,1), area 47.4mm2, adj f7,f9,f12,f330
  f330: torus R=11.83mm, axis (0,0,-1), area 5.2mm2, adj f2,f6,f13,f329
  f331: cylinder r=0.4mm len=2.2mm, axis (-0.92,0.38,0), area 1.4mm2, adj f2,f13,f332,f337
  f332: torus R=0.6mm, axis (0,0,-1), area 0.3mm2, adj f2,f331,f334,f336
  f333: cylinder r=0.4mm len=9.1mm, axis (-1,0,0), area 5.5mm2, adj f2,f72,f78,f295
  f334: cylinder r=0.4mm len=0.86mm, axis (0,-1,0), area 0.5mm2, adj f1,f2,f332,f335
  f335: plane 4.9x0.86mm, normal (-1,0,0), area 4.2mm2, adj f0,f1,f334,f336
  f336: cylinder r=0.2mm len=4.9mm, axis (0,0,1), area 1.2mm2, adj f0,f332,f335,f337
  f337: plane 6.68x4.2mm, normal (-0.38,-0.92,0), area 23.9mm2, adj f0,f11,f12,f13,f331,f336,f338
  f338: torus R=13.6mm, axis (0,0,-1), area 13.7mm2, adj f0,f11,f14,f15,f337,f339
  f339: plane 6.68x4.2mm, normal (0.38,-0.92,0), area 23.9mm2, adj f0,f5,f6,f7,f14,f338,f340
  f340: cylinder r=0.2mm len=4.9mm, axis (0,0,1), area 1.2mm2, adj f0,f4,f339,f341
  f341: plane 4.9x0.86mm, normal (1,0,0), area 4.2mm2, adj f0,f3,f340,f342
  f342: plane 5.3x1mm, normal (0,-1,0), area 5.3mm2, adj f0,f2,f3,f341,f343
  f343: cylinder r=0.2mm len=5.3mm, axis (0,0,-1), area 1.7mm2, adj f0,f2,f342,f344
  f344: plane 11.25x10.79mm, normal (1,0,0), area 81mm2, adj f0,f2,f75,f76,f78,f343,f345
  f345: cylinder r=0.4mm len=8.3mm, axis (1,0,0), area 5.2mm2, adj f0,f75,f344,f346
  f346: plane 11.25x10.99mm, normal (-1,0,0), area 82mm2, adj f0,f1,f2,f72,f73,f75,f345
PLACE A t=(-85.4,99.56,0)mm fixed
PLACE B t=(-85.4,99.56,0.26)mm
MATE slider B.f247 <-> A.f3  axis (0,0,1) through (-85.4,99.56,150.66)mm
